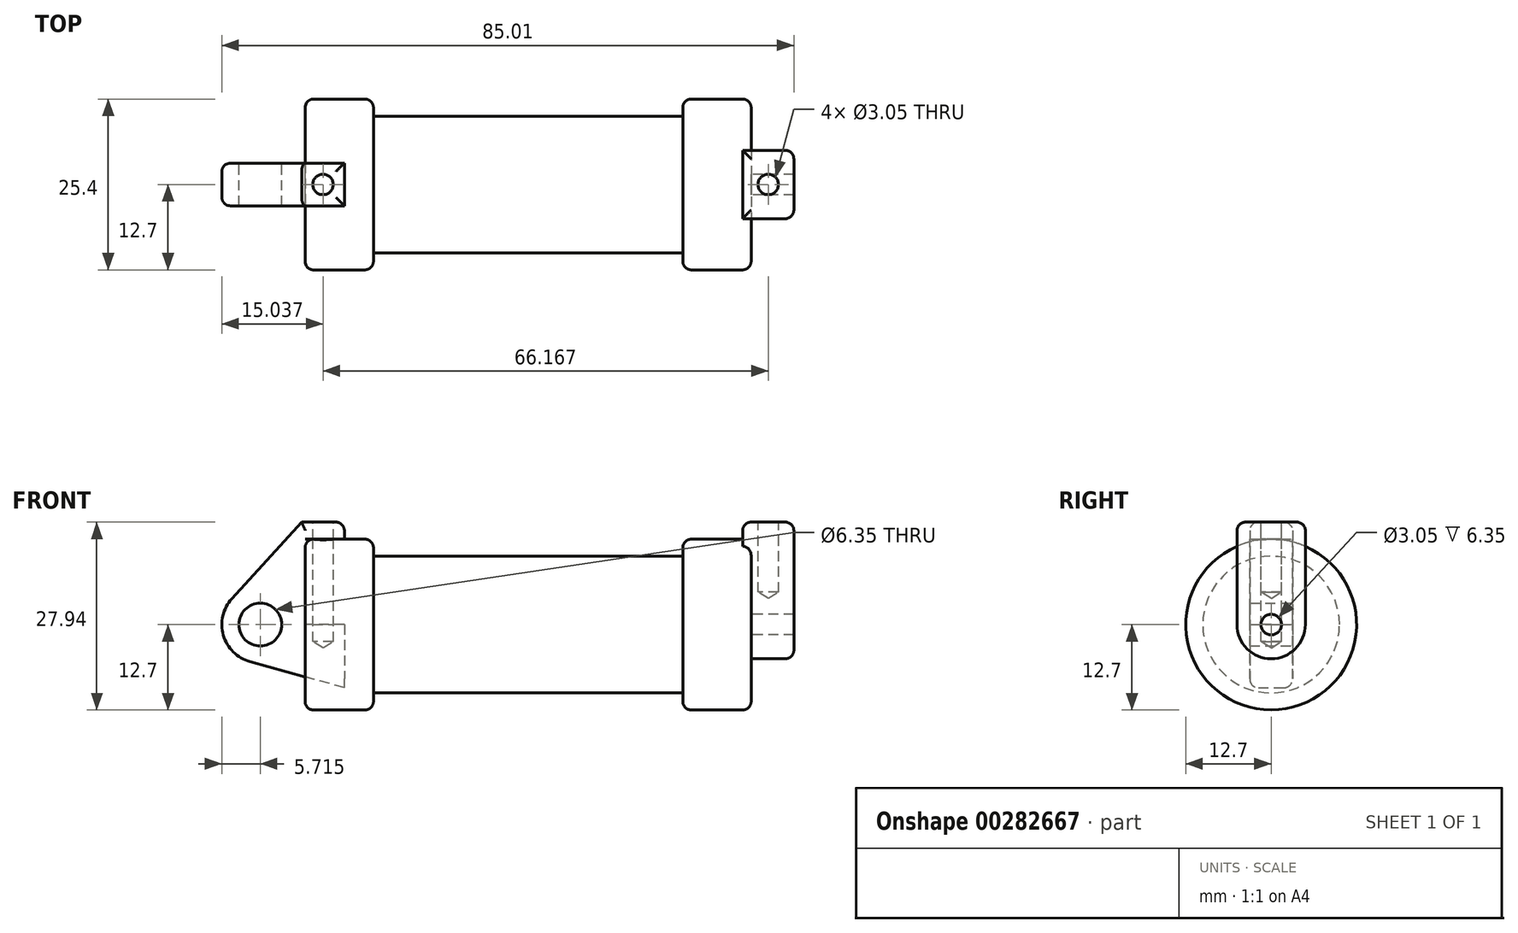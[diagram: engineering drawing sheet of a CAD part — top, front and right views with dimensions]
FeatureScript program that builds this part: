
annotation { "Feature Type Name" : "Feature", "Feature Type Description" : "" }
export const myFeature = defineFeature(function(context is Context, id is Id, definition is map)
    precondition{}
    {
        {
            var Q0;
            Q0=qCreatedBy(makeId("Front.planeOp"),FACE);
            var sketch = newSketch(context, id + "F0", { "sketchPlane" : qUnion([Q0])});
            skLineSegment(sketch, "E0", {"start": v(0, 0) * mm, "end": v(0, 12.7) * mm});
            skLineSegment(sketch, "E1", {"start": v(0, 12.7) * mm, "end": v(10.16, 12.7) * mm});
            skLineSegment(sketch, "E2", {"start": v(10.16, 12.7) * mm, "end": v(10.16, 10.16) * mm});
            skLineSegment(sketch, "E3", {"start": v(10.16, 10.16) * mm, "end": v(56.13, 10.16) * mm});
            skLineSegment(sketch, "E4", {"start": v(56.13, 10.16) * mm, "end": v(56.13, 12.7) * mm});
            skLineSegment(sketch, "E5", {"start": v(56.13, 12.7) * mm, "end": v(66.3, 12.7) * mm});
            skLineSegment(sketch, "E6", {"start": v(66.3, 12.7) * mm, "end": v(66.3, 0) * mm});
            skLineSegment(sketch, "E7", {"start": v(66.3, 0) * mm, "end": v(0, 0) * mm});
            skLineSegment(sketch, "E8", {"start": v(5.84, 15.24) * mm, "end": v(-0.5, 15.24) * mm});
            skLineSegment(sketch, "E9", {"start": v(-0.5, 15.24) * mm, "end": v(-10.88, 3.85) * mm});
            skLineSegment(sketch, "E10", {"start": v(0, 0) * mm, "end": v(-6.65, 0) * mm});
            skCircle(sketch, "E11", {"center": v(-6.65, 0) * mm, "radius": 5.72 * mm});
            skCircle(sketch, "E12", {"center": v(-6.65, 0) * mm, "radius": 3.18 * mm});
            skLineSegment(sketch, "E13", {"start": v(5.84, 15.24) * mm, "end": v(5.84, -9.4) * mm});
            skLineSegment(sketch, "E14", {"start": v(5.84, -9.4) * mm, "end": v(-8.18, -5.5) * mm});
            skLineSegment(sketch, "E15", {"start": v(5.84, 0) * mm, "end": v(71.71, 0) * mm, "construction": true});
            skLineSegment(sketch, "E16", {"start": v(85.33, 0) * mm, "end": v(5.84, 0) * mm, "construction": true});
            skSolve(sketch);
        }
        {
            var Q0;
            {var subQ0=sQuery(id+"F0.wireOp",EDGE,"E2");Q0=makeQuery(id+"F0.imprint","IMPRINT",FACE,{"disambiguationData":[TD([[makeQuery(id+"F0.imprint","IMPRINT",EDGE,{"derivedFrom":subQ0}),-1.0]])]});}
            var Q1;
            {var subQ0=sQuery(id+"F0.wireOp",EDGE,"E0");Q1=makeQuery(id+"F0.imprint","IMPRINT",FACE,{"disambiguationData":[TD([[makeQuery(id+"F0.imprint","IMPRINT",EDGE,{"derivedFrom":subQ0}),-1.0]])]});}
            var Q2;
            Q2=sQuery(id+"F0.wireOp",EDGE,"E7");
            revolve(context, id + "F1", {"entities" : qUnion([Q0, Q1]), "axis" : qUnion([Q2]), "revolveType" : RevolveType.FULL});
        }
        {
            var Q0;
            Q0=makeQuery(id+"F0.imprint","IMPRINT",FACE,{"disambiguationData":[TD([[makeQuery(id+"F0.imprint","IMPRINT",EDGE,{"derivedFrom":sQuery(id+"F0.wireOp",EDGE,"E12")}),-1.0]])]});
            var Q1;
            {var subQ0=sQuery(id+"F0.wireOp",EDGE,"E14");Q1=makeQuery(id+"F0.imprint","IMPRINT",FACE,{"disambiguationData":[TD([[makeQuery(id+"F0.imprint","IMPRINT",EDGE,{"derivedFrom":subQ0}),-1.0]])]});}
            var Q2;
            {var subQ1=sQuery(id+"F0.wireOp",EDGE,"E0");Q2=makeQuery(id+"F0.imprint","IMPRINT",FACE,{"disambiguationData":[TD([[makeQuery(id+"F0.imprint","IMPRINT",EDGE,{"derivedFrom":subQ1}),1.0]])]});}
            extrude(context, id + "F2", {"entities" : qUnion([Q0, Q1, Q2]), "endBound" : BoundingType.SYMMETRIC, "depth" : 6.35 * mm});
        }
        {
            var Q0;
            Q0=makeQuery(id+"F1.opRevolve","SWEPT_FACE",FACE,{"disambiguationData":[OSD([sQuery(id+"F0.wireOp",EDGE,"E6")])]});
            var sketch = newSketch(context, id + "F3", { "sketchPlane" : qUnion([Q0])});
            skCircle(sketch, "E17", {"center": v(0, 0) * mm, "radius": 1.52 * mm});
            skCircle(sketch, "E18", {"center": v(0, 0) * mm, "radius": 5.08 * mm});
            skLineSegment(sketch, "E19", {"start": v(-5.08, 0) * mm, "end": v(-5.08, 15.24) * mm});
            skLineSegment(sketch, "E20", {"start": v(5.08, 0) * mm, "end": v(5.08, 15.24) * mm});
            skLineSegment(sketch, "E21", {"start": v(-5.08, 15.24) * mm, "end": v(5.08, 15.24) * mm});
            skSolve(sketch);
        }
        {
            var Q0;
            {var subQ0=sQuery(id+"F3.wireOp",EDGE,"E19");var subQ1=sQuery(id+"F3.wireOp",EDGE,"E18");var subQ2=makeQuery(id+"F3.imprint","INTERSECT",VERTEX,{"derivedFrom":[subQ1,subQ0]});Q0=makeQuery(id+"F3.imprint","IMPRINT",FACE,{"disambiguationData":[TD([[makeQuery(id+"F3.imprint","IMPRINT",EDGE,{"disambiguationData":[TD([[subQ2,1.0]])],"derivedFrom":subQ1}),-1.0]])]});}
            var Q1;
            {var subQ0=sQuery(id+"F3.wireOp",EDGE,"E21");Q1=makeQuery(id+"F3.imprint","IMPRINT",FACE,{"disambiguationData":[TD([[makeQuery(id+"F3.imprint","IMPRINT",EDGE,{"derivedFrom":subQ0}),-1.0]])]});}
            var Q2;
            Q2=makeQuery(id+"F3.imprint","IMPRINT",FACE,{"disambiguationData":[TD([[makeQuery(id+"F3.imprint","IMPRINT",EDGE,{"derivedFrom":sQuery(id+"F3.wireOp",EDGE,"E17")}),-1.0]])]});
            extrude(context, id + "F4", {"entities" : qUnion([Q0, Q1, Q2]), "operationType" : NewBodyOperationType.ADD, "oppositeDirection" : true, "depth" : 1.27 * mm});
        }
        {
            var Q0;
            Q0=makeQuery(id+"F3.imprint","IMPRINT",FACE,{"disambiguationData":[TD([[makeQuery(id+"F3.imprint","IMPRINT",EDGE,{"derivedFrom":sQuery(id+"F3.wireOp",EDGE,"E17")}),-1.0]])]});
            var Q1;
            {var subQ0=sQuery(id+"F3.wireOp",EDGE,"E19");var subQ1=sQuery(id+"F3.wireOp",EDGE,"E18");var subQ2=makeQuery(id+"F3.imprint","INTERSECT",VERTEX,{"derivedFrom":[subQ1,subQ0]});Q1=makeQuery(id+"F3.imprint","IMPRINT",FACE,{"disambiguationData":[TD([[makeQuery(id+"F3.imprint","IMPRINT",EDGE,{"disambiguationData":[TD([[subQ2,1.0]])],"derivedFrom":subQ1}),-1.0]])]});}
            var Q2;
            {var subQ0=sQuery(id+"F3.wireOp",EDGE,"E21");Q2=makeQuery(id+"F3.imprint","IMPRINT",FACE,{"disambiguationData":[TD([[makeQuery(id+"F3.imprint","IMPRINT",EDGE,{"derivedFrom":subQ0}),-1.0]])]});}
            extrude(context, id + "F5", {"entities" : qUnion([Q0, Q1, Q2]), "operationType" : NewBodyOperationType.ADD, "depth" : 6.35 * mm});
        }
        {
            var Q0;
            Q0=makeQuery(id+"F5.opExtrude","CAP_EDGE",EDGE,{"disambiguationData":[OSD([sQuery(id+"F3.wireOp",EDGE,"E21")])],"isStart":false});
            var Q1;
            {var subQ0=sQuery(id+"F3.wireOp",EDGE,"E21");var subQ1=sQuery(id+"F3.wireOp",EDGE,"E20");Q1=makeQuery(id+"F5.boolean.opBoolean","MERGE",EDGE,{"derivedFrom":[makeQuery(id+"F4.opExtrude","SWEPT_EDGE",EDGE,{"disambiguationData":[OSD([subQ1,subQ0])]}),makeQuery(id+"F5.opExtrude","SWEPT_EDGE",EDGE,{"disambiguationData":[OSD([subQ1,subQ0])]})]});}
            var Q2;
            {var subQ0=sQuery(id+"F3.wireOp",EDGE,"E21");var subQ1=sQuery(id+"F3.wireOp",EDGE,"E19");Q2=makeQuery(id+"F5.boolean.opBoolean","MERGE",EDGE,{"derivedFrom":[makeQuery(id+"F4.opExtrude","SWEPT_EDGE",EDGE,{"disambiguationData":[OSD([subQ1,subQ0])]}),makeQuery(id+"F5.opExtrude","SWEPT_EDGE",EDGE,{"disambiguationData":[OSD([subQ1,subQ0])]})]});}
            var Q3;
            Q3=makeQuery(id+"F1.opRevolve","SWEPT_EDGE",EDGE,{"disambiguationData":[OSD([sQuery(id+"F0.wireOp",EDGE,"E5"),sQuery(id+"F0.wireOp",EDGE,"E6")])]});
            var Q4;
            Q4=makeQuery(id+"F1.opRevolve","SWEPT_EDGE",EDGE,{"disambiguationData":[OSD([sQuery(id+"F0.wireOp",EDGE,"E4"),sQuery(id+"F0.wireOp",EDGE,"E5")])]});
            var Q5;
            Q5=makeQuery(id+"F4.opExtrude","CAP_EDGE",EDGE,{"disambiguationData":[OSD([sQuery(id+"F3.wireOp",EDGE,"E21")])],"isStart":false});
            var Q6;
            Q6=makeQuery(id+"F5.opExtrude","CAP_EDGE",EDGE,{"disambiguationData":[OSD([sQuery(id+"F3.wireOp",EDGE,"E18")])],"isStart":false});
            var Q7;
            Q7=makeQuery(id+"F2.opExtrude","CAP_EDGE",EDGE,{"disambiguationData":[OSD([sQuery(id+"F0.wireOp",EDGE,"E11")])],"isStart":false});
            var Q8;
            Q8=makeQuery(id+"F2.opExtrude","CAP_EDGE",EDGE,{"disambiguationData":[OSD([sQuery(id+"F0.wireOp",EDGE,"E9")])],"isStart":false});
            var Q9;
            Q9=makeQuery(id+"F2.opExtrude","CAP_EDGE",EDGE,{"disambiguationData":[OSD([sQuery(id+"F0.wireOp",EDGE,"E9")])],"isStart":true});
            var Q10;
            Q10=makeQuery(id+"F2.opExtrude","CAP_EDGE",EDGE,{"disambiguationData":[OSD([sQuery(id+"F0.wireOp",EDGE,"E11")])],"isStart":true});
            var Q11;
            Q11=makeQuery(id+"F2.opExtrude","CAP_EDGE",EDGE,{"disambiguationData":[OSD([sQuery(id+"F0.wireOp",EDGE,"E8")])],"isStart":true});
            var Q12;
            Q12=makeQuery(id+"F2.opExtrude","CAP_EDGE",EDGE,{"disambiguationData":[OSD([sQuery(id+"F0.wireOp",EDGE,"E8")])],"isStart":false});
            var Q13;
            Q13=makeQuery(id+"F2.opExtrude","SWEPT_EDGE",EDGE,{"disambiguationData":[OSD([sQuery(id+"F0.wireOp",EDGE,"E8"),sQuery(id+"F0.wireOp",EDGE,"E13")])]});
            var Q14;
            Q14=makeQuery(id+"F1.opRevolve","SWEPT_FACE",FACE,{"disambiguationData":[OSD([sQuery(id+"F0.wireOp",EDGE,"E0")])]});
            var Q15;
            Q15=makeQuery(id+"F1.opRevolve","SWEPT_EDGE",EDGE,{"disambiguationData":[OSD([sQuery(id+"F0.wireOp",EDGE,"E1"),sQuery(id+"F0.wireOp",EDGE,"E2")])]});
            fillet(context, id + "F6", {"entities" : qUnion([Q0, Q1, Q2, Q3, Q4, Q5, Q6, Q7, Q8, Q9, Q10, Q11, Q12, Q13, Q14, Q15]), "radius" : 1.27 * mm, "tangentPropagation" : true, "allowEdgeOverflow" : false});
        }
        {
            var Q0;
            Q0=makeQuery(id+"F2.opExtrude","SWEPT_FACE",FACE,{"disambiguationData":[OSD([sQuery(id+"F0.wireOp",EDGE,"E8")])]});
            var sketch = newSketch(context, id + "F7", { "sketchPlane" : qUnion([Q0])});
            skCircle(sketch, "E22", {"center": v(2.67, 0) * mm, "radius": 1.52 * mm});
            skPoint(sketch, "E22.centerSnap0", {"position": v(5.84, 0) * mm});
            skPoint(sketch, "E22.centerSnap1", {"position": v(2.67, 3.18) * mm});
            skSolve(sketch);
        }
        {
            var Q0;
            {var subQ0=sQuery(id+"F3.wireOp",EDGE,"E21");Q0=makeQuery(id+"F5.boolean.opBoolean","MERGE",FACE,{"derivedFrom":[makeQuery(id+"F4.opExtrude","SWEPT_FACE",FACE,{"disambiguationData":[OSD([subQ0])]}),makeQuery(id+"F5.opExtrude","SWEPT_FACE",FACE,{"disambiguationData":[OSD([subQ0])]})]});}
            var sketch = newSketch(context, id + "F8", { "sketchPlane" : qUnion([Q0])});
            skCircle(sketch, "E23", {"center": v(68.83, 0) * mm, "radius": 1.52 * mm});
            skPoint(sketch, "E23.centerSnap0", {"position": v(65.02, 0) * mm});
            skPoint(sketch, "E23.centerSnap1", {"position": v(68.83, 5.08) * mm});
            skSolve(sketch);
        }
        {
            var Q0;
            Q0=sQuery(id+"F7.wireOp",VERTEX,"E22.center");
            var Q1;
            Q1=makeQuery(id+"F1.opRevolve","SWEPT_BODY",BODY,{"disambiguationData":[OSD([sQuery(id+"F0.wireOp",EDGE,"E0"),sQuery(id+"F0.wireOp",EDGE,"E1"),sQuery(id+"F0.wireOp",EDGE,"E2"),sQuery(id+"F0.wireOp",EDGE,"E3"),sQuery(id+"F0.wireOp",EDGE,"E4"),sQuery(id+"F0.wireOp",EDGE,"E5"),sQuery(id+"F0.wireOp",EDGE,"E6"),sQuery(id+"F0.wireOp",EDGE,"E7")])]});
            var Q2;
            Q2=makeQuery(id+"F2.opExtrude","SWEPT_BODY",BODY,{"disambiguationData":[OSD([sQuery(id+"F0.wireOp",EDGE,"E0"),sQuery(id+"F0.wireOp",EDGE,"E1"),sQuery(id+"F0.wireOp",EDGE,"E7"),sQuery(id+"F0.wireOp",EDGE,"E8"),sQuery(id+"F0.wireOp",EDGE,"E9"),sQuery(id+"F0.wireOp",EDGE,"E11"),sQuery(id+"F0.wireOp",EDGE,"E12"),sQuery(id+"F0.wireOp",EDGE,"E13"),sQuery(id+"F0.wireOp",EDGE,"E14")])]});
            hole(context, id + "F9", {"style" : HoleStyle.SIMPLE, "endStyle" : HoleEndStyle.BLIND, "holeDiameter" : 3.05 * mm, "holeDepth" : 17.78 * mm, "tappedDepth" : 12.7 * mm, "tapClearance" : 3, "locations" : qUnion([Q0]), "scope" : qUnion([Q1, Q2])});
        }
        {
            var Q0;
            Q0=sQuery(id+"F8.wireOp",VERTEX,"E23.center");
            var Q1;
            Q1=makeQuery(id+"F1.opRevolve","SWEPT_BODY",BODY,{"disambiguationData":[OSD([sQuery(id+"F0.wireOp",EDGE,"E0"),sQuery(id+"F0.wireOp",EDGE,"E1"),sQuery(id+"F0.wireOp",EDGE,"E2"),sQuery(id+"F0.wireOp",EDGE,"E3"),sQuery(id+"F0.wireOp",EDGE,"E4"),sQuery(id+"F0.wireOp",EDGE,"E5"),sQuery(id+"F0.wireOp",EDGE,"E6"),sQuery(id+"F0.wireOp",EDGE,"E7")])]});
            hole(context, id + "F10", {"style" : HoleStyle.SIMPLE, "endStyle" : HoleEndStyle.BLIND, "holeDiameter" : 3.05 * mm, "holeDepth" : 10.4 * mm, "tappedDepth" : 12.7 * mm, "tapClearance" : 3, "locations" : qUnion([Q0]), "scope" : qUnion([Q1])});
        }
    });
